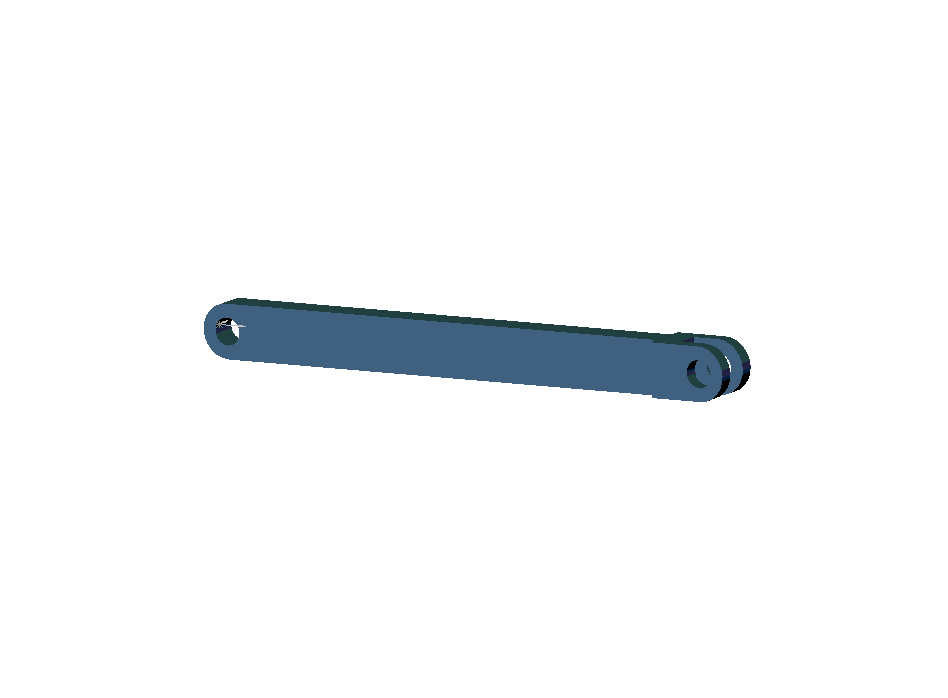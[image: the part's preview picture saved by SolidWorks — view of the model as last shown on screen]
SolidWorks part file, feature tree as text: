
SOLIDWORKS PART (.sldprt)
format: sldprt  version: not decoded by parser v0  size: 117,760 bytes
history: native  units: mm
features: plane x3, sketch x3, cut_extrude x2, fillet x2, material x1, extrude x1 (+9 scaffold rows collapsed)
feature tree (21):
  scaffold x9  (default folders/planes/origin — collapsed)
  material  "Material <not specified>"
  plane  "Plane1"
  plane  "Plane2"
  plane  "Plane3"
  sketch  "Sketch1"  dims[c1.D1=170.0mm c1.D2=10.0mm c2.D1=10.0mm c2.D3=190.0mm c2.D4=4.0mm c3.D1=5.0mm c3.D5=5.0mm c3.D6=220.0mm c3.D7=200.0mm]
  extrude  "Base-Extrude"  Depth=20mm
  sketch  "Sketch5"  dims[D1=10.0mm]
  cut_extrude  "Cut-Extrude2"  [1 undecoded]
  sketch  "Sketch6"  dims[D1=10.0mm]
  cut_extrude  "Cut-Extrude3"  [1 undecoded]
  fillet  "Fillet1"  Radius=10mm
  fillet  "Fillet2"  Radius=10mm
decode coverage: 6 of 8 modeling features carry decoded parameters
note: 2 parameter values undecoded
note: suppression state not decoded; provenance and decode notes live in map.json
